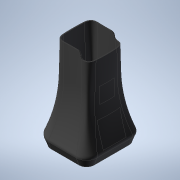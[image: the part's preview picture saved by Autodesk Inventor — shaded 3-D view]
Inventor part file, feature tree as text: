
AUTODESK INVENTOR PART (.ipt)
format: ipt  version: 2021 (Build 250183000, 183)  size: 2,707,968 bytes
history: native  units: mm
features: other x25, sketch x23, plane x16, projected_geometry x6, extrude x5, hole x4, fillet x3, loft x1, shell x1, mirror x1
ambient origin geometry x8: Origin, YZ Plane, XZ Plane, XY Plane, X Axis, Y Axis, Z Axis, Center Point
bodies: Body1 (feature_tree), Body2 (feature_tree), Body3 (feature_tree), Body4 (feature_tree), Body5 (feature_tree), Body6 (feature_tree)
feature tree (85):
  other  "實體1"
  extrude  "擠出1"  Depth=284.5mm
  plane  "工作平面1"
  sketch  "草圖2"
  plane  "工作平面8"
  sketch  "草圖10"
  plane  "工作平面9"
  sketch  "草圖12"
  plane  "工作平面10"
  sketch  "草圖13"
  plane  "工作平面11"
  sketch  "草圖14"
  plane  "工作平面12"
  sketch  "草圖15"
  plane  "工作平面13"
  sketch  "草圖16"
  plane  "工作平面14"
  sketch  "草圖17"
  plane  "工作平面15"
  loft  "斷面混成1"
  shell  "薄殼1"  Thickness=50.0mm
  hole  "孔1"  [1 undecoded]
  plane  "工作平面16"
  other  "分割1"
  hole  "孔2"  [1 undecoded]
  hole  "孔3"  [1 undecoded]
  extrude  "擠出3"  Depth=225.0mm
  fillet  "圓角1"  Radius=50.0mm
  extrude  "擠出4"  Depth=400.0mm
  hole  "孔6"  [1 undecoded]
  extrude  "擠出6"  Depth=10.0mm
  fillet  "圓角2"  Radius=25.0mm
  plane  "工作平面17"
  plane  "工作平面29"
  plane  "工作平面30"
  other  "凸轂4"
  plane  "工作平面31"
  other  "凸轂5"
  mirror  "鏡射13"
  other  "分割4"
  other  "直接編輯1"
  extrude  "擠出36"  Depth=400.0mm
  fillet  "圓角4"  Radius=800.0mm
  plane  "工作平面35"
  sketch  "草圖1"
  sketch  "草圖18"
  sketch  "草圖19"
  sketch  "草圖20"
  other  "Srf2"
  sketch  "草圖21"
  projected_geometry  "投影迴路3"
  sketch  "草圖22"
  projected_geometry  "投影迴路4"
  sketch  "草圖24"
  projected_geometry  "投影迴路10"
  sketch  "草圖25"
  projected_geometry  "投影迴路11"
  sketch  "草圖29"
  projected_geometry  "投影迴路14"
  sketch  "草圖30"
  sketch  "草圖86"
  other  "Srf5"
  sketch  "草圖87"
  sketch  "草圖88"
  sketch  "草圖93"
  other  "Srf6"
  sketch  "草圖94"
  projected_geometry  "投影迴路75"
  plane  "工作平面34"
  other  "擠出表面2"
  other  "擠出表面5"
  other  "擠出表面6"
  other  "投影切割邊5"
  other  "投影切割邊7"
  other  "投影切割邊8"
  other  "投影切割邊9"
  other  "投影切割邊10"
  other  "投影切割邊11"
  other  "投影切割邊12"
  other  "投影切割邊13"
  other  "實體2"
  other  "實體3"
  other  "實體12"
  other  "實體13"
  other  "移動1"
note: 4 required parameter values undecoded (feature->parameter linkage not recoverable at this tier; creation-order binding heuristic only, values carry confidence <= 0.55)
